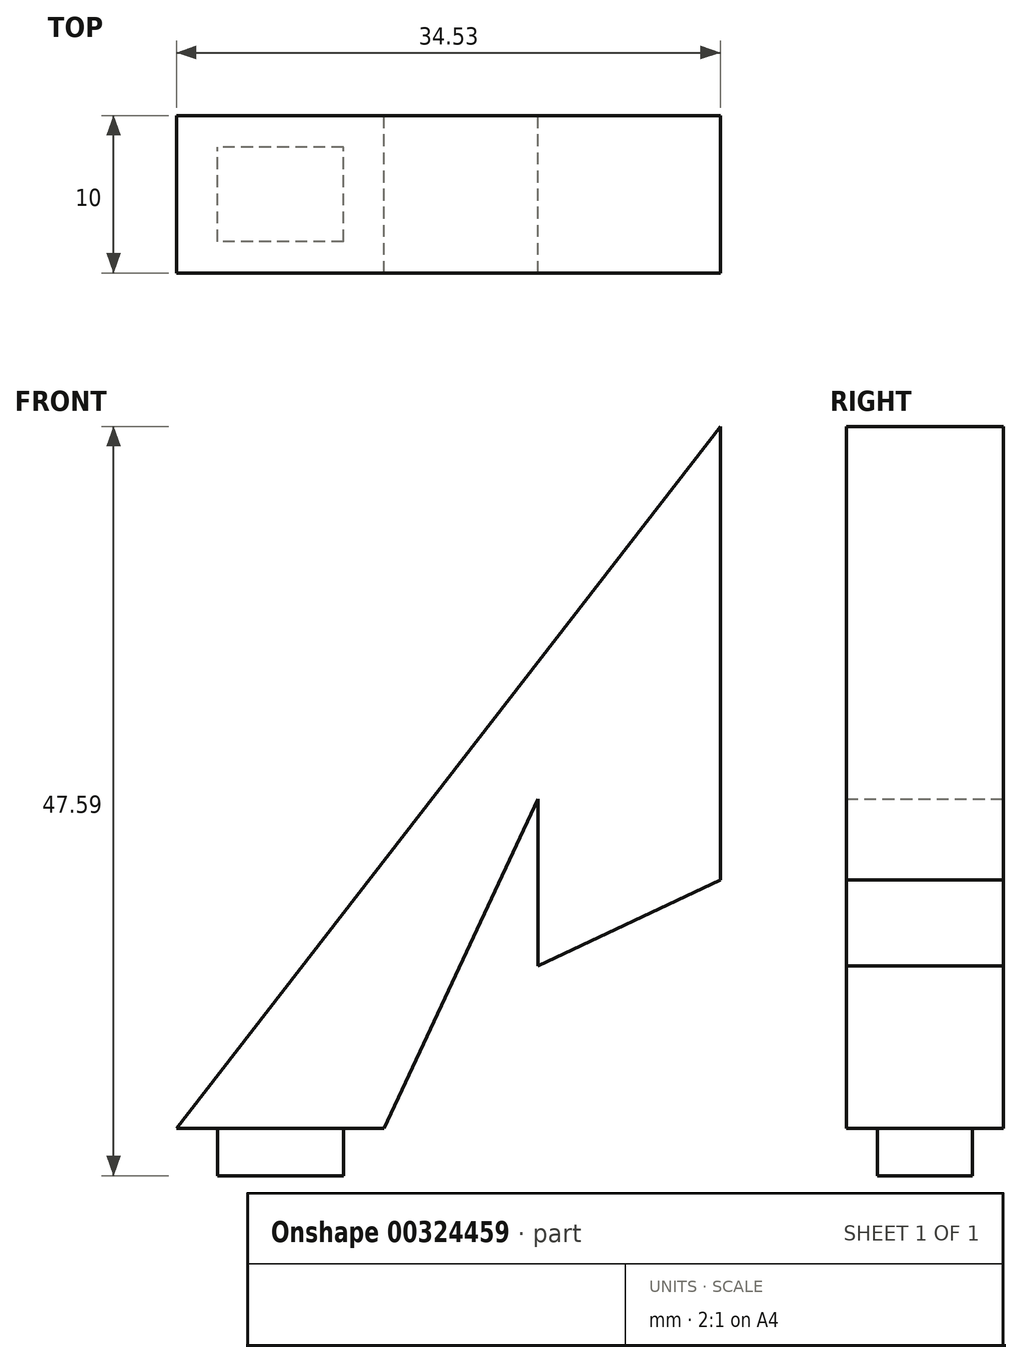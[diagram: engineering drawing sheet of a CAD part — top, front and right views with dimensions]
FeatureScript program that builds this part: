
annotation { "Feature Type Name" : "Feature", "Feature Type Description" : "" }
export const myFeature = defineFeature(function(context is Context, id is Id, definition is map)
    precondition{}
    {
        {
            var Q0;
            Q0=qCreatedBy(makeId("Front.planeOp"),FACE);
            var sketch = newSketch(context, id + "F0", { "sketchPlane" : qUnion([Q0])});
            skLineSegment(sketch, "E0", {"start": v(0, 0) * mm, "end": v(13.19, 0) * mm});
            skLineSegment(sketch, "E1", {"start": v(13.19, 0) * mm, "end": v(22.95, 20.94) * mm});
            skLineSegment(sketch, "E2", {"start": v(22.95, 20.94) * mm, "end": v(22.95, 10.34) * mm});
            skLineSegment(sketch, "E3", {"start": v(22.95, 10.34) * mm, "end": v(34.53, 15.8) * mm});
            skLineSegment(sketch, "E4", {"start": v(34.53, 15.8) * mm, "end": v(34.53, 44.6) * mm});
            skLineSegment(sketch, "E5", {"start": v(34.53, 44.6) * mm, "end": v(0, 0) * mm});
            skSolve(sketch);
        }
        {
            var Q0;
            Q0 = qSketchRegion(id + "F0", true);
            extrude(context, id + "F1", {"entities" : qUnion([Q0]), "depth" : 10 * mm});
        }
        {
            var Q0;
            Q0=makeQuery(id+"F1.opExtrude","SWEPT_FACE",FACE,{"disambiguationData":[OSD([sQuery(id+"F0.wireOp",EDGE,"E0")])]});
            var sketch = newSketch(context, id + "F2", { "sketchPlane" : qUnion([Q0])});
            skLineSegment(sketch, "E6", {"start": v(6.6, 10) * mm, "end": v(6.6, 0) * mm});
            skLineSegment(sketch, "E7", {"start": v(0, 5) * mm, "end": v(13.19, 5) * mm});
            skLineSegment(sketch, "E8.bottom", {"start": v(10.6, 8) * mm, "end": v(2.6, 8) * mm});
            skLineSegment(sketch, "E8.top", {"start": v(10.6, 2) * mm, "end": v(2.6, 2) * mm});
            skLineSegment(sketch, "E8.left", {"start": v(10.6, 8) * mm, "end": v(10.6, 2) * mm});
            skLineSegment(sketch, "E8.right", {"start": v(2.6, 8) * mm, "end": v(2.6, 2) * mm});
            skPoint(sketch, "E8.middle", {"position": v(6.6, 5) * mm});
            skSolve(sketch);
        }
        {
            var Q0;
            Q0 = qSketchRegion(id + "F2", true);
            extrude(context, id + "F3", {"entities" : qUnion([Q0]), "operationType" : NewBodyOperationType.ADD, "depth" : 3 * mm});
        }
    });
